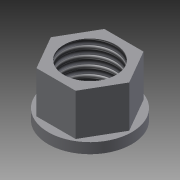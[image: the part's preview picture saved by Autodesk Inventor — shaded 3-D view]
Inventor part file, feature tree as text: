
AUTODESK INVENTOR PART (.ipt)
format: ipt  version: 2015 (Build 190159000, 159)  size: 99,328 bytes
history: native  units: mm
features: extrude x3, sketch x3, thread x1
ambient origin geometry x8: Origin, YZ Plane, XZ Plane, XY Plane, X Axis, Y Axis, Z Axis, Center Point
bodies: 实体1 (feature_tree)
feature tree (7):
  extrude  "拉伸1"  Depth=1.0mm TaperAngle=0.0deg
  extrude  "拉伸2"  Depth=4.0mm TaperAngle=0.0deg
  extrude  "拉伸3"  Depth=4.0mm TaperAngle=0.0deg
  thread  "螺纹1"  [1 undecoded]
  sketch  "草图1"  dims[d0=8.0mm d1=1.0mm d2=0.0mm]
  sketch  "草图2"  dims[d3=6.5mm d4=4.0mm d5=0.0mm]
  sketch  "草图3"  dims[d6=5.0mm d7=4.0mm d8=0.0mm d9=10.0mm d10=0.0mm]
note: 1 required parameter value undecoded (feature->parameter linkage not recoverable at this tier; creation-order binding heuristic only, values carry confidence <= 0.55)
